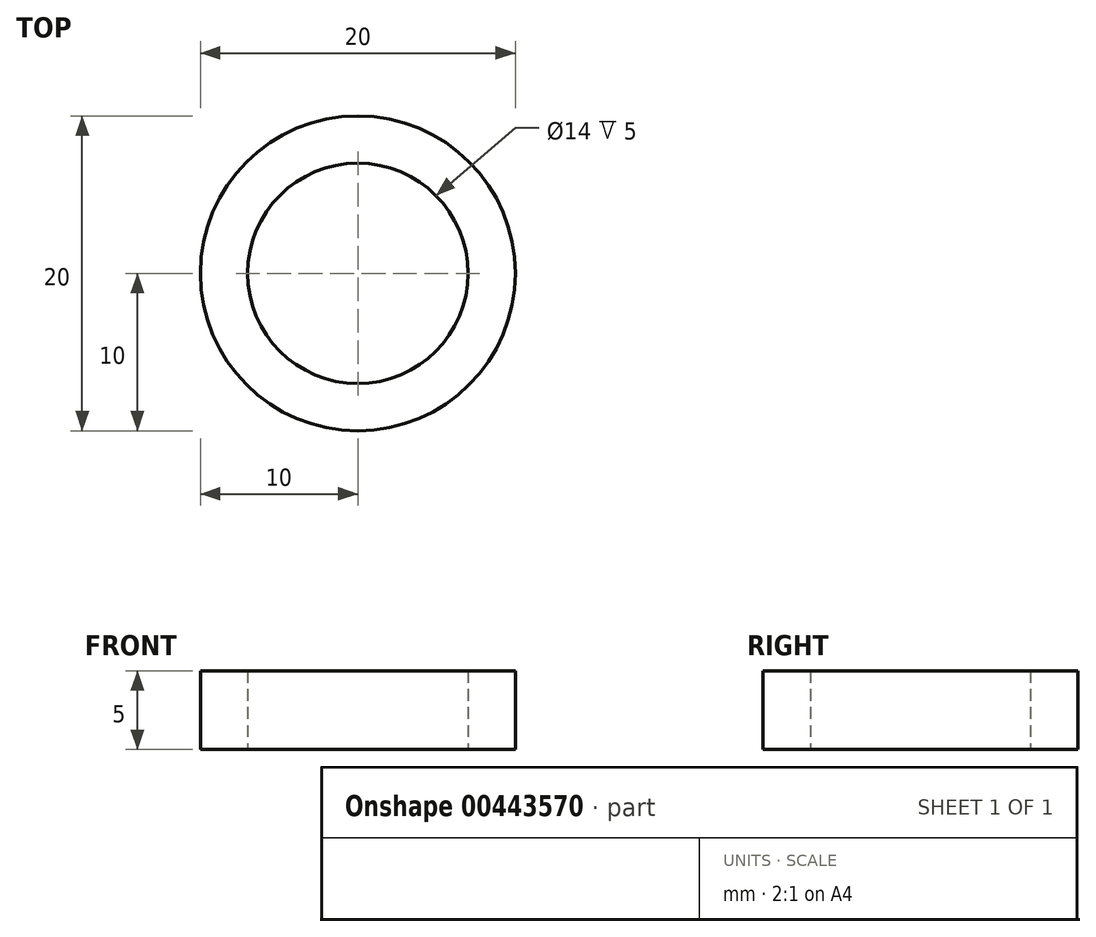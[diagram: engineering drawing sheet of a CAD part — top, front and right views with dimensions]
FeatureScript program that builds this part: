
annotation { "Feature Type Name" : "Feature", "Feature Type Description" : "" }
export const myFeature = defineFeature(function(context is Context, id is Id, definition is map)
    precondition{}
    {
        {
            var Q0;
            Q0=qCreatedBy(makeId("Top.planeOp"),FACE);
            var sketch = newSketch(context, id + "F0", { "sketchPlane" : qUnion([Q0])});
            skCircle(sketch, "E0", {"center": v(0, 0) * mm, "radius": 10 * mm});
            skCircle(sketch, "E1", {"center": v(0, 0) * mm, "radius": 7 * mm});
            skCircle(sketch, "E2", {"center": v(0, 0) * mm, "radius": 0.25 * mm});
            skCircle(sketch, "E3", {"center": v(1, 0) * mm, "radius": 0.25 * mm});
            skCircle(sketch, "E4", {"center": v(-1, 0) * mm, "radius": 0.25 * mm});
            skLineSegment(sketch, "E5", {"start": v(-1, 0) * mm, "end": v(0, 0) * mm});
            skLineSegment(sketch, "E6", {"start": v(0, 0) * mm, "end": v(1, 0) * mm});
            skSolve(sketch);
        }
        {
            var Q0;
            Q0=makeQuery(id+"F0.imprint","IMPRINT",FACE,{"disambiguationData":[TD([[makeQuery(id+"F0.imprint","IMPRINT",EDGE,{"derivedFrom":sQuery(id+"F0.wireOp",EDGE,"E0")}),1.0]])]});
            extrude(context, id + "F1", {"entities" : qUnion([Q0]), "depth" : 5 * mm});
        }
    });
